# Revit family: LAMP_SUSPENSION RIGIDA 9621XXX
name_source: partatom
category: Modelos genéricos
revit_build: Autodesk Revit LT 2015 (Build: 20140606_1530(x64)
units: mm (PartAtom-declared; Revit-internal decimal feet)

## types (2) — shared parameters
Accessory type = Suspension
Available lengths = 100mm, 250mm, 500mm, 1000mm
Comentarios de tipo = Availability of switching between accessories through visibility parameters when placed in a project.
Dimensions = Ø84mm x 37mm
Fabricante = LAMP LIGHTING
Last update = 23/02/2018
Manufacturer URL = http://www.lamp.es
Manufacturer country = Spain
Spain
Manufacturer name = LAMP LIGHTING
Model explanation = Availability of switching between accessories through visibility parameters when placed in a project.
Product URL = http://www.lamp.es
Product datasheet (1000mm) = http://admin.lamp.es
Product datasheet (100mm) = http://admin.lamp.es
Product datasheet (250mm) = http://admin.lamp.es
Product datasheet (500mm) = http://admin.lamp.es

## per-type parameters (varying)
| type | Descripción (1000mm) | Descripción (100mm) | Descripción (250mm) | Descripción (500mm) | Finish | Material Florón | Modelo (1000mm) | Modelo (100mm) | Modelo (250mm) | Modelo (500mm) | Product code (1000mm) | Product code (100mm) | Product code (250mm) | Product code (500mm) |
| WHITE | ACC. ELECMEC RIGID SUSP 1000MM WH. | ACC. ELECMEC RIGID SUSP 100MM WH. | ACC. ELECMEC RIGID SUSP 250MM WH. | ACC. ELECMEC RIGID SUSP 500MM WH. | Shiny white | LAMP_Plástico genérico BL | 9621100 | 9621010 | 9621020 | 9621050 | 9621100 | 9621010 | 9621020 | 9621050 |
| GREY | ACC. ELECMEC RIGID SUSP 1000MM GR. | ACC. ELECMEC RIGID SUSP 100MM GR. | ACC. ELECMEC RIGID SUSP 250MM GR. | ACC. ELECMEC RIGID SUSP 500MM GR. | Bright silver grey | LAMP_Plástico genérico GR | 9621103 | 9621013 | 9621023 | 9621053 | 9621103 | 9621013 | 9621023 | 9621053 |
